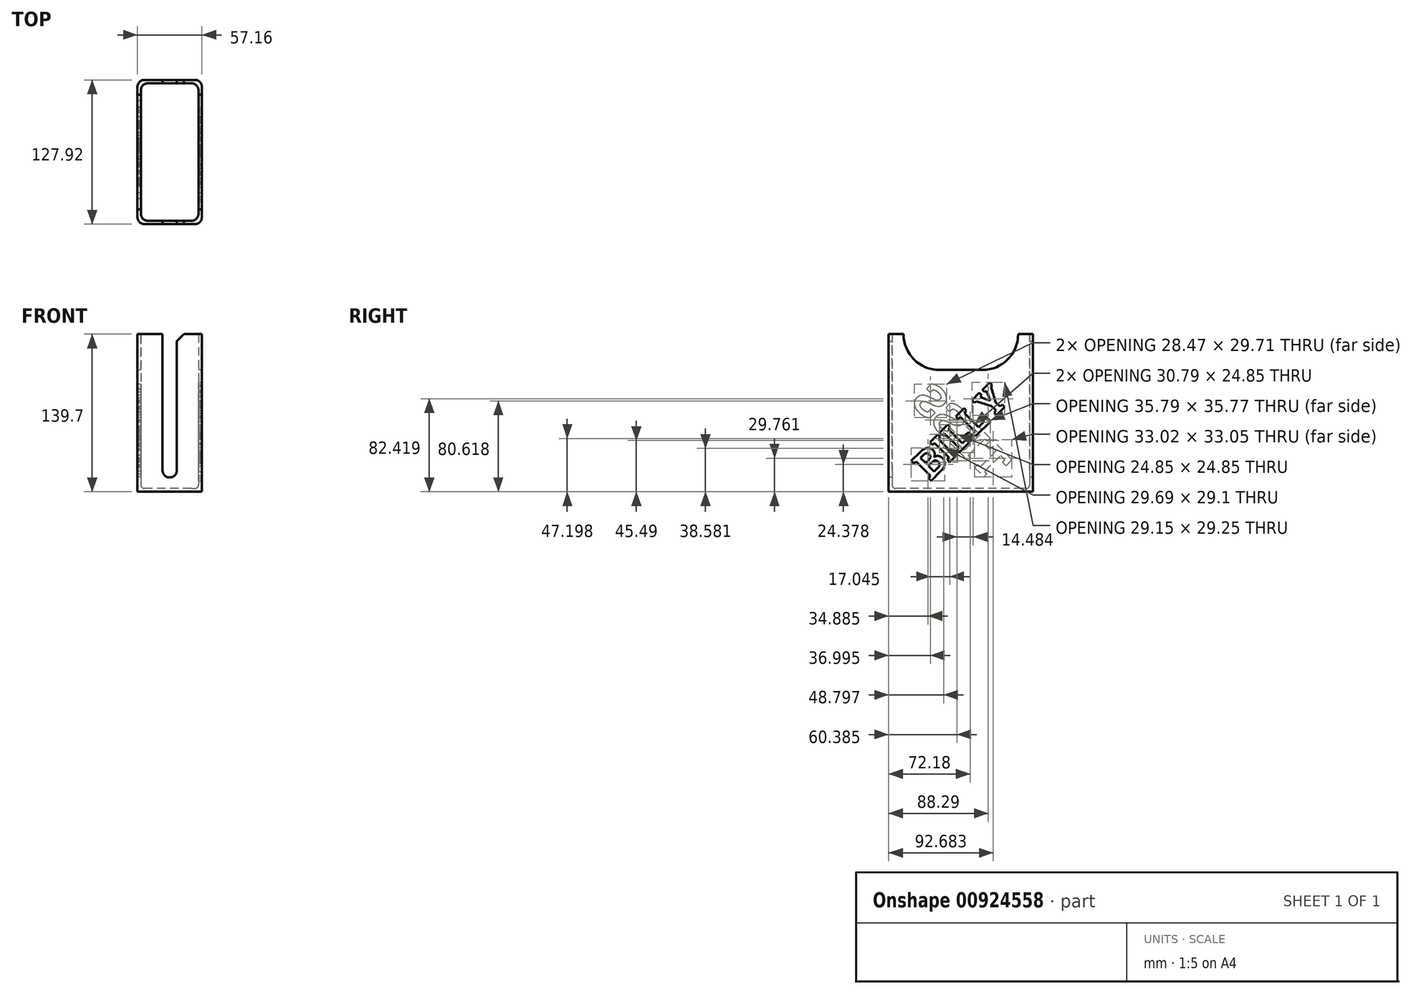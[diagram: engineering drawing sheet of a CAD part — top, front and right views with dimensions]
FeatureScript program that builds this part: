
annotation { "Feature Type Name" : "Feature", "Feature Type Description" : "" }
export const myFeature = defineFeature(function(context is Context, id is Id, definition is map)
    precondition{}
    {
        {
            var Q0;
            Q0=qCreatedBy(makeId("Top.planeOp"),FACE);
            var sketch = newSketch(context, id + "F0", { "sketchPlane" : qUnion([Q0])});
            skLineSegment(sketch, "E0.bottom", {"start": v(28.58, 63.96) * mm, "end": v(-28.57, 63.96) * mm});
            skLineSegment(sketch, "E0.top", {"start": v(28.58, -63.96) * mm, "end": v(-28.58, -63.96) * mm});
            skLineSegment(sketch, "E0.left", {"start": v(28.58, 63.96) * mm, "end": v(28.58, -63.96) * mm});
            skLineSegment(sketch, "E0.right", {"start": v(-28.58, 63.96) * mm, "end": v(-28.58, -63.96) * mm});
            skPoint(sketch, "E0.middle", {"position": v(0, 0) * mm});
            skSolve(sketch);
        }
        {
            var Q0;
            Q0=makeQuery(id+"F0.imprint","IMPRINT",FACE,{"disambiguationData":[TD([[makeQuery(id+"F0.imprint","IMPRINT",EDGE,{"derivedFrom":sQuery(id+"F0.wireOp",EDGE,"E0.bottom")}),1.0]])]});
            extrude(context, id + "F1", {"entities" : qUnion([Q0]), "depth" : 139.7 * mm, "offsetDistance" : 25.4 * mm});
        }
        {
            var Q0;
            Q0=makeQuery(id+"F1.opExtrude","CAP_FACE",FACE,{"disambiguationData":[OSD([sQuery(id+"F0.wireOp",EDGE,"E0.bottom"),sQuery(id+"F0.wireOp",EDGE,"E0.top"),sQuery(id+"F0.wireOp",EDGE,"E0.left"),sQuery(id+"F0.wireOp",EDGE,"E0.right")])],"isStart":false});
            shell(context, id + "F2", {"entities" : qUnion([Q0]), "thickness" : 3 * mm});
        }
        {
            var Q0;
            Q0=makeQuery(id+"F1.opExtrude","CAP_FACE",FACE,{"disambiguationData":[OSD([sQuery(id+"F0.wireOp",EDGE,"E0.bottom"),sQuery(id+"F0.wireOp",EDGE,"E0.top"),sQuery(id+"F0.wireOp",EDGE,"E0.left"),sQuery(id+"F0.wireOp",EDGE,"E0.right")])],"isStart":false});
            var sketch = newSketch(context, id + "F3", { "sketchPlane" : qUnion([Q0])});
            skLineSegment(sketch, "E1.bottom", {"start": v(-6.35, 63.96) * mm, "end": v(6.35, 63.96) * mm});
            skLineSegment(sketch, "E1.top", {"start": v(-6.35, -63.96) * mm, "end": v(6.35, -63.96) * mm});
            skLineSegment(sketch, "E1.left", {"start": v(-6.35, 63.96) * mm, "end": v(-6.35, -63.96) * mm});
            skLineSegment(sketch, "E1.right", {"start": v(6.35, 63.96) * mm, "end": v(6.35, -63.96) * mm});
            skPoint(sketch, "E1.middle", {"position": v(0, 0) * mm});
            skSolve(sketch);
        }
        {
            var Q0;
            {var subQ0=sQuery(id+"F3.wireOp",EDGE,"E1.left");var subQ1=sQuery(id+"F0.wireOp",EDGE,"E0.bottom");var subQ2=makeQuery(id+"F2.opShell","OFFSET_EDGE",EDGE,{"disambiguationData":[OSD([subQ1]),TDD([makeQuery(id+"F1.opExtrude","CAP_EDGE",EDGE,{"disambiguationData":[OSD([subQ1])],"isStart":false})])]});var subQ3=makeQuery(id+"F3.imprint","INTERSECT",VERTEX,{"derivedFrom":[subQ2,subQ0]});Q0=makeQuery(id+"F3.imprint","IMPRINT",FACE,{"disambiguationData":[TD([[makeQuery(id+"F3.imprint","IMPRINT",EDGE,{"disambiguationData":[TD([[subQ3,-1.0]])],"derivedFrom":subQ0}),1.0]])]});}
            var Q1;
            {var subQ0=sQuery(id+"F3.wireOp",EDGE,"E1.top");Q1=makeQuery(id+"F3.imprint","IMPRINT",FACE,{"disambiguationData":[TD([[makeQuery(id+"F3.imprint","IMPRINT",EDGE,{"derivedFrom":subQ0}),-1.0]])]});}
            var Q2;
            {var subQ0=sQuery(id+"F3.wireOp",EDGE,"E1.bottom");Q2=makeQuery(id+"F3.imprint","IMPRINT",FACE,{"disambiguationData":[TD([[makeQuery(id+"F3.imprint","IMPRINT",EDGE,{"derivedFrom":subQ0}),1.0]])]});}
            var Q3;
            {var subQ7=sQuery(id+"F0.wireOp",EDGE,"E0.left");var subQ8=makeQuery(id+"F2.opShell","OFFSET_EDGE",EDGE,{"disambiguationData":[OSD([subQ7]),TDD([makeQuery(id+"F1.opExtrude","CAP_EDGE",EDGE,{"disambiguationData":[OSD([subQ7])],"isStart":false})])]});Q3=makeQuery(id+"F3.imprint","IMPRINT",FACE,{"disambiguationData":[TD([[makeQuery(id+"F3.imprint","IMPRINT",EDGE,{"derivedFrom":subQ8}),-1.0]])]});}
            var Q4;
            Q4=makeQuery(id+"F2.opShell","OFFSET_FACE",FACE,{"disambiguationData":[OSD([sQuery(id+"F0.wireOp",EDGE,"E0.bottom"),sQuery(id+"F0.wireOp",EDGE,"E0.top"),sQuery(id+"F0.wireOp",EDGE,"E0.left"),sQuery(id+"F0.wireOp",EDGE,"E0.right")])]});
            extrude(context, id + "F4", {"entities" : qUnion([Q0, Q1, Q2, Q3]), "operationType" : NewBodyOperationType.REMOVE, "oppositeDirection" : true, "depth" : 127 * mm, "endBoundEntityFace" : qUnion([Q4]), "offsetDistance" : 25.4 * mm});
        }
        {
            var Q0;
            {var subQ0=sQuery(id+"F3.wireOp",EDGE,"E1.left");var subQ2=sQuery(id+"F0.wireOp",EDGE,"E0.top");Q0=makeQuery(id+"F4.boolean.opBoolean","COPY",EDGE,{"disambiguationData":[TD([makeQuery(id+"F1.opExtrude","SWEPT_FACE",FACE,{"disambiguationData":[OSD([subQ2])]})])],"derivedFrom":makeQuery(id+"F4.opExtrude","CAP_EDGE",EDGE,{"disambiguationData":[OSD([subQ0])],"isStart":false})});}
            var Q1;
            {var subQ0=sQuery(id+"F3.wireOp",EDGE,"E1.right");var subQ1=sQuery(id+"F0.wireOp",EDGE,"E0.top");var subQ2=makeQuery(id+"F1.opExtrude","CAP_EDGE",EDGE,{"disambiguationData":[OSD([subQ1])],"isStart":false});Q1=makeQuery(id+"F4.boolean.opBoolean","COPY",EDGE,{"derivedFrom":makeQuery(id+"F4.opExtrude","CAP_EDGE",EDGE,{"disambiguationData":[OSD([subQ0]),TDD([makeQuery(id+"F3.imprint","IMPRINT",EDGE,{"disambiguationData":[TD([[makeQuery(id+"F3.imprint","INTERSECT",VERTEX,{"derivedFrom":[makeQuery(id+"F2.opShell","OFFSET_EDGE",EDGE,{"disambiguationData":[OSD([subQ1]),TDD([subQ2])]}),subQ0]}),-1.0]])],"derivedFrom":subQ0})])],"isStart":false})});}
            var Q2;
            {var subQ2=sQuery(id+"F0.wireOp",EDGE,"E0.bottom");var subQ3=sQuery(id+"F3.wireOp",EDGE,"E1.left");Q2=makeQuery(id+"F4.boolean.opBoolean","COPY",EDGE,{"disambiguationData":[TD([makeQuery(id+"F1.opExtrude","SWEPT_FACE",FACE,{"disambiguationData":[OSD([subQ2])]})])],"derivedFrom":makeQuery(id+"F4.opExtrude","CAP_EDGE",EDGE,{"disambiguationData":[OSD([subQ3])],"isStart":false})});}
            var Q3;
            {var subQ0=sQuery(id+"F3.wireOp",EDGE,"E1.right");var subQ1=sQuery(id+"F0.wireOp",EDGE,"E0.bottom");var subQ2=makeQuery(id+"F1.opExtrude","CAP_EDGE",EDGE,{"disambiguationData":[OSD([subQ1])],"isStart":false});Q3=makeQuery(id+"F4.boolean.opBoolean","COPY",EDGE,{"derivedFrom":makeQuery(id+"F4.opExtrude","CAP_EDGE",EDGE,{"disambiguationData":[OSD([subQ0]),TDD([makeQuery(id+"F3.imprint","IMPRINT",EDGE,{"disambiguationData":[TD([[makeQuery(id+"F3.imprint","INTERSECT",VERTEX,{"derivedFrom":[makeQuery(id+"F2.opShell","OFFSET_EDGE",EDGE,{"disambiguationData":[OSD([subQ1]),TDD([subQ2])]}),subQ0]}),1.0]])],"derivedFrom":subQ0})])],"isStart":false})});}
            fillet(context, id + "F5", {"entities" : qUnion([Q0, Q1, Q2, Q3]), "radius" : 6.35 * mm, "tangentPropagation" : true, "allowEdgeOverflow" : false});
        }
        {
            var Q0;
            Q0=makeQuery(id+"F1.opExtrude","SWEPT_FACE",FACE,{"disambiguationData":[OSD([sQuery(id+"F0.wireOp",EDGE,"E0.right")])]});
            var sketch = newSketch(context, id + "F6", { "sketchPlane" : qUnion([Q0])});
            skLineSegment(sketch, "E2.bottom", {"start": v(50.8, 107.95) * mm, "end": v(-50.8, 107.95) * mm});
            skLineSegment(sketch, "E2.top", {"start": v(50.8, 139.7) * mm, "end": v(-50.8, 139.7) * mm});
            skLineSegment(sketch, "E2.left", {"start": v(50.8, 107.95) * mm, "end": v(50.8, 139.7) * mm});
            skLineSegment(sketch, "E2.right", {"start": v(-50.8, 107.95) * mm, "end": v(-50.8, 139.7) * mm});
            skPoint(sketch, "E2.middle", {"position": v(0, 123.83) * mm});
            skSolve(sketch);
        }
        {
            var Q0;
            {var subQ0=sQuery(id+"F6.wireOp",EDGE,"E2.top");Q0=makeQuery(id+"F6.imprint","IMPRINT",FACE,{"disambiguationData":[TD([[makeQuery(id+"F6.imprint","IMPRINT",EDGE,{"derivedFrom":subQ0}),1.0]])]});}
            var Q1;
            {var subQ0=sQuery(id+"F6.wireOp",EDGE,"E2.bottom");Q1=makeQuery(id+"F6.imprint","IMPRINT",FACE,{"disambiguationData":[TD([[makeQuery(id+"F6.imprint","IMPRINT",EDGE,{"derivedFrom":subQ0}),-1.0]])]});}
            extrude(context, id + "F7", {"entities" : qUnion([Q0, Q1]), "operationType" : NewBodyOperationType.REMOVE, "endBound" : BoundingType.THROUGH_ALL, "oppositeDirection" : true, "depth" : 25.4 * mm, "offsetDistance" : 25.4 * mm});
        }
        {
            var Q0;
            {var subQ0=sQuery(id+"F0.wireOp",EDGE,"E0.right");var subQ1=sQuery(id+"F6.wireOp",EDGE,"E2.bottom");var subQ2=sQuery(id+"F6.wireOp",EDGE,"E2.right");Q0=makeQuery(id+"F7.boolean.opBoolean","COPY",EDGE,{"disambiguationData":[TD([makeQuery(id+"F1.opExtrude","SWEPT_FACE",FACE,{"disambiguationData":[OSD([subQ0])]})])],"derivedFrom":makeQuery(id+"F7.opExtrude","SWEPT_EDGE",EDGE,{"disambiguationData":[OSD([subQ1,subQ2])]})});}
            var Q1;
            {var subQ0=sQuery(id+"F0.wireOp",EDGE,"E0.left");var subQ1=sQuery(id+"F6.wireOp",EDGE,"E2.bottom");var subQ2=sQuery(id+"F6.wireOp",EDGE,"E2.right");Q1=makeQuery(id+"F7.boolean.opBoolean","COPY",EDGE,{"disambiguationData":[TD([makeQuery(id+"F1.opExtrude","SWEPT_FACE",FACE,{"disambiguationData":[OSD([subQ0])]})])],"derivedFrom":makeQuery(id+"F7.opExtrude","SWEPT_EDGE",EDGE,{"disambiguationData":[OSD([subQ1,subQ2])]})});}
            var Q2;
            {var subQ0=sQuery(id+"F0.wireOp",EDGE,"E0.left");var subQ1=sQuery(id+"F6.wireOp",EDGE,"E2.bottom");var subQ2=sQuery(id+"F6.wireOp",EDGE,"E2.left");Q2=makeQuery(id+"F7.boolean.opBoolean","COPY",EDGE,{"disambiguationData":[TD([makeQuery(id+"F1.opExtrude","SWEPT_FACE",FACE,{"disambiguationData":[OSD([subQ0])]})])],"derivedFrom":makeQuery(id+"F7.opExtrude","SWEPT_EDGE",EDGE,{"disambiguationData":[OSD([subQ1,subQ2])]})});}
            var Q3;
            {var subQ0=sQuery(id+"F0.wireOp",EDGE,"E0.right");var subQ1=sQuery(id+"F6.wireOp",EDGE,"E2.bottom");var subQ2=sQuery(id+"F6.wireOp",EDGE,"E2.left");Q3=makeQuery(id+"F7.boolean.opBoolean","COPY",EDGE,{"disambiguationData":[TD([makeQuery(id+"F1.opExtrude","SWEPT_FACE",FACE,{"disambiguationData":[OSD([subQ0])]})])],"derivedFrom":makeQuery(id+"F7.opExtrude","SWEPT_EDGE",EDGE,{"disambiguationData":[OSD([subQ1,subQ2])]})});}
            fillet(context, id + "F8", {"entities" : qUnion([Q0, Q1, Q2, Q3]), "radius" : 31.75 * mm, "tangentPropagation" : true, "allowEdgeOverflow" : false});
        }
        {
            var Q0;
            {var subQ0=sQuery(id+"F0.wireOp",EDGE,"E0.right");Q0=makeQuery(id+"F2.opShell","OFFSET_EDGE",EDGE,{"disambiguationData":[OSD([subQ0]),TDD([makeQuery(id+"F1.opExtrude","CAP_EDGE",EDGE,{"disambiguationData":[OSD([subQ0])],"isStart":true})])]});}
            var Q1;
            {var subQ0=sQuery(id+"F0.wireOp",EDGE,"E0.right");var subQ3=sQuery(id+"F0.wireOp",EDGE,"E0.bottom");Q1=makeQuery(id+"F4.boolean.opBoolean","SPLIT",EDGE,{"disambiguationData":[TD([makeQuery(id+"F2.opShell","OFFSET_FACE",FACE,{"disambiguationData":[OSD([subQ0])]})])],"derivedFrom":makeQuery(id+"F2.opShell","OFFSET_EDGE",EDGE,{"disambiguationData":[OSD([subQ3]),TDD([makeQuery(id+"F1.opExtrude","CAP_EDGE",EDGE,{"disambiguationData":[OSD([subQ3])],"isStart":true})])]})});}
            var Q2;
            {var subQ0=sQuery(id+"F0.wireOp",EDGE,"E0.left");Q2=makeQuery(id+"F2.opShell","OFFSET_EDGE",EDGE,{"disambiguationData":[OSD([subQ0]),TDD([makeQuery(id+"F1.opExtrude","CAP_EDGE",EDGE,{"disambiguationData":[OSD([subQ0])],"isStart":true})])]});}
            var Q3;
            {var subQ2=sQuery(id+"F0.wireOp",EDGE,"E0.left");var subQ3=sQuery(id+"F0.wireOp",EDGE,"E0.top");Q3=makeQuery(id+"F4.boolean.opBoolean","SPLIT",EDGE,{"disambiguationData":[TD([makeQuery(id+"F2.opShell","OFFSET_FACE",FACE,{"disambiguationData":[OSD([subQ2])]})])],"derivedFrom":makeQuery(id+"F2.opShell","OFFSET_EDGE",EDGE,{"disambiguationData":[OSD([subQ3]),TDD([makeQuery(id+"F1.opExtrude","CAP_EDGE",EDGE,{"disambiguationData":[OSD([subQ3])],"isStart":true})])]})});}
            fillet(context, id + "F9", {"entities" : qUnion([Q0, Q1, Q2, Q3]), "radius" : 3.17 * mm, "tangentPropagation" : true, "allowEdgeOverflow" : false});
        }
        {
            var Q0;
            {var subQ0=sQuery(id+"F0.wireOp",EDGE,"E0.right");var subQ1=sQuery(id+"F0.wireOp",EDGE,"E0.top");Q0=makeQuery(id+"FaH29F3IyYW9KPR_1.boolean.opBoolean","MERGE",EDGE,{"derivedFrom":[makeQuery(id+"F1.opExtrude","SWEPT_EDGE",EDGE,{"disambiguationData":[OSD([subQ1,subQ0])]}),makeQuery(id+"FaH29F3IyYW9KPR_1.opExtrude","SWEPT_EDGE",EDGE,{"disambiguationData":[OSD([subQ1,subQ0])]})]});}
            var Q1;
            {var subQ0=sQuery(id+"F0.wireOp",EDGE,"E0.left");var subQ1=sQuery(id+"F0.wireOp",EDGE,"E0.top");Q1=makeQuery(id+"FaH29F3IyYW9KPR_1.boolean.opBoolean","MERGE",EDGE,{"derivedFrom":[makeQuery(id+"F1.opExtrude","SWEPT_EDGE",EDGE,{"disambiguationData":[OSD([subQ1,subQ0])]}),makeQuery(id+"FaH29F3IyYW9KPR_1.opExtrude","SWEPT_EDGE",EDGE,{"disambiguationData":[OSD([subQ1,subQ0])]})]});}
            var Q2;
            {var subQ0=sQuery(id+"F0.wireOp",EDGE,"E0.left");var subQ1=sQuery(id+"F0.wireOp",EDGE,"E0.bottom");Q2=makeQuery(id+"FaH29F3IyYW9KPR_1.boolean.opBoolean","MERGE",EDGE,{"derivedFrom":[makeQuery(id+"F1.opExtrude","SWEPT_EDGE",EDGE,{"disambiguationData":[OSD([subQ1,subQ0])]}),makeQuery(id+"FaH29F3IyYW9KPR_1.opExtrude","SWEPT_EDGE",EDGE,{"disambiguationData":[OSD([subQ1,subQ0])]})]});}
            var Q3;
            {var subQ0=sQuery(id+"F0.wireOp",EDGE,"E0.right");var subQ1=sQuery(id+"F0.wireOp",EDGE,"E0.bottom");Q3=makeQuery(id+"FaH29F3IyYW9KPR_1.boolean.opBoolean","MERGE",EDGE,{"derivedFrom":[makeQuery(id+"F1.opExtrude","SWEPT_EDGE",EDGE,{"disambiguationData":[OSD([subQ1,subQ0])]}),makeQuery(id+"FaH29F3IyYW9KPR_1.opExtrude","SWEPT_EDGE",EDGE,{"disambiguationData":[OSD([subQ1,subQ0])]})]});}
            var Q4;
            Q4=makeQuery(id+"F2.opShell","OFFSET_EDGE",EDGE,{"disambiguationData":[OSD([sQuery(id+"F0.wireOp",EDGE,"E0.bottom"),sQuery(id+"F0.wireOp",EDGE,"E0.right")])]});
            var Q5;
            Q5=makeQuery(id+"F2.opShell","OFFSET_EDGE",EDGE,{"disambiguationData":[OSD([sQuery(id+"F0.wireOp",EDGE,"E0.bottom"),sQuery(id+"F0.wireOp",EDGE,"E0.left")])]});
            var Q6;
            Q6=makeQuery(id+"F2.opShell","OFFSET_EDGE",EDGE,{"disambiguationData":[OSD([sQuery(id+"F0.wireOp",EDGE,"E0.top"),sQuery(id+"F0.wireOp",EDGE,"E0.right")])]});
            var Q7;
            Q7=makeQuery(id+"F2.opShell","OFFSET_EDGE",EDGE,{"disambiguationData":[OSD([sQuery(id+"F0.wireOp",EDGE,"E0.top"),sQuery(id+"F0.wireOp",EDGE,"E0.left")])]});
            fillet(context, id + "F10", {"entities" : qUnion([Q0, Q1, Q2, Q3, Q4, Q5, Q6, Q7]), "radius" : 6.35 * mm, "tangentPropagation" : true, "allowEdgeOverflow" : false});
        }
        {
            var Q0;
            {var subQ0=sQuery(id+"F0.wireOp",EDGE,"E0.top");var subQ1=sQuery(id+"F3.wireOp",EDGE,"E1.left");Q0=makeQuery(id+"F4.boolean.opBoolean","COPY",EDGE,{"disambiguationData":[TD([makeQuery(id+"F1.opExtrude","SWEPT_FACE",FACE,{"disambiguationData":[OSD([subQ0])]})])],"derivedFrom":makeQuery(id+"F4.opExtrude","CAP_EDGE",EDGE,{"disambiguationData":[OSD([subQ1])],"isStart":true})});}
            var Q1;
            {var subQ0=sQuery(id+"F3.wireOp",EDGE,"E1.right");var subQ1=sQuery(id+"F0.wireOp",EDGE,"E0.top");var subQ2=makeQuery(id+"F1.opExtrude","CAP_EDGE",EDGE,{"disambiguationData":[OSD([subQ1])],"isStart":false});Q1=makeQuery(id+"F4.boolean.opBoolean","COPY",EDGE,{"derivedFrom":makeQuery(id+"F4.opExtrude","CAP_EDGE",EDGE,{"disambiguationData":[OSD([subQ0]),TDD([makeQuery(id+"F3.imprint","IMPRINT",EDGE,{"disambiguationData":[TD([[makeQuery(id+"F3.imprint","INTERSECT",VERTEX,{"derivedFrom":[makeQuery(id+"F2.opShell","OFFSET_EDGE",EDGE,{"disambiguationData":[OSD([subQ1]),TDD([subQ2])]}),subQ0]}),-1.0]])],"derivedFrom":subQ0})])],"isStart":true})});}
            var Q2;
            {var subQ0=sQuery(id+"F0.wireOp",EDGE,"E0.bottom");var subQ1=sQuery(id+"F3.wireOp",EDGE,"E1.left");Q2=makeQuery(id+"F4.boolean.opBoolean","COPY",EDGE,{"disambiguationData":[TD([makeQuery(id+"F1.opExtrude","SWEPT_FACE",FACE,{"disambiguationData":[OSD([subQ0])]})])],"derivedFrom":makeQuery(id+"F4.opExtrude","CAP_EDGE",EDGE,{"disambiguationData":[OSD([subQ1])],"isStart":true})});}
            var Q3;
            {var subQ0=sQuery(id+"F3.wireOp",EDGE,"E1.right");var subQ1=sQuery(id+"F0.wireOp",EDGE,"E0.bottom");var subQ2=makeQuery(id+"F1.opExtrude","CAP_EDGE",EDGE,{"disambiguationData":[OSD([subQ1])],"isStart":false});Q3=makeQuery(id+"F4.boolean.opBoolean","COPY",EDGE,{"derivedFrom":makeQuery(id+"F4.opExtrude","CAP_EDGE",EDGE,{"disambiguationData":[OSD([subQ0]),TDD([makeQuery(id+"F3.imprint","IMPRINT",EDGE,{"disambiguationData":[TD([[makeQuery(id+"F3.imprint","INTERSECT",VERTEX,{"derivedFrom":[makeQuery(id+"F2.opShell","OFFSET_EDGE",EDGE,{"disambiguationData":[OSD([subQ1]),TDD([subQ2])]}),subQ0]}),1.0]])],"derivedFrom":subQ0})])],"isStart":true})});}
            chamfer(context, id + "F11", {"entities" : qUnion([Q0, Q1, Q2, Q3]), "width" : 6.35 * mm, "tangentPropagation" : true});
        }
        {
            var Q0;
            Q0=makeQuery(id+"F1.opExtrude","SWEPT_FACE",FACE,{"disambiguationData":[OSD([sQuery(id+"F0.wireOp",EDGE,"E0.left")])]});
            var sketch = newSketch(context, id + "F12", { "sketchPlane" : qUnion([Q0])});
            skText(sketch, "E3", { "text": "BILLY", "fontName": "RobotoSlab-Bold.ttf"});
            skPoint(sketch, "E4", {"position": v(0, 53.98) * mm});
            skLineSegment(sketch, "E5", {"start": v(0, 107.95) * mm, "end": v(0, 0) * mm, "construction": true});
            skLineSegment(sketch, "E6", {"start": v(0, 53.98) * mm, "end": v(-57.6, 53.98) * mm, "construction": true});
            skLineSegment(sketch, "E7", {"start": v(0, 53.98) * mm, "end": v(57.6, 53.98) * mm, "construction": true});
            const initialGuessF12  = {"E3": [-0.02702, 0.00915, 0.7071, 0.7071, 0.02517]};
            skSetInitialGuess(sketch, initialGuessF12);
            skSolve(sketch);
        }
        {
            var Q0;
            Q0 = qSketchRegion(id + "F12", true);
            var Q1;
            Q1=makeQuery(id+"F2.opShell","OFFSET_FACE",FACE,{"disambiguationData":[OSD([sQuery(id+"F0.wireOp",EDGE,"E0.left")])]});
            extrude(context, id + "F13", {"entities" : qUnion([Q0]), "operationType" : NewBodyOperationType.REMOVE, "endBound" : BoundingType.UP_TO_SURFACE, "oppositeDirection" : true, "depth" : 25.4 * mm, "endBoundEntityFace" : qUnion([Q1]), "offsetDistance" : 25.4 * mm});
        }
        {
            var Q0;
            Q0=makeQuery(id+"F1.opExtrude","SWEPT_FACE",FACE,{"disambiguationData":[OSD([sQuery(id+"F0.wireOp",EDGE,"E0.right")])]});
            var sketch = newSketch(context, id + "F14", { "sketchPlane" : qUnion([Q0])});
            skText(sketch, "E8", { "text": "TESS", "fontName": "RobotoSlab-Bold.ttf"});
            skPoint(sketch, "E9", {"position": v(0, 53.98) * mm});
            skLineSegment(sketch, "E10", {"start": v(0, 107.95) * mm, "end": v(0, 0) * mm, "construction": true});
            skLineSegment(sketch, "E11", {"start": v(0, 53.98) * mm, "end": v(-57.6, 53.98) * mm, "construction": true});
            skLineSegment(sketch, "E12", {"start": v(0, 53.98) * mm, "end": v(57.6, 53.98) * mm, "construction": true});
            const initialGuessF14  = {"E8": [-0.0258, 0.00794, 0.7071, 0.7071, 0.02862]};
            skSetInitialGuess(sketch, initialGuessF14);
            skSolve(sketch);
        }
        {
            var Q0;
            Q0 = qSketchRegion(id + "F14", true);
            var Q1;
            Q1=makeQuery(id+"F2.opShell","OFFSET_FACE",FACE,{"disambiguationData":[OSD([sQuery(id+"F0.wireOp",EDGE,"E0.right")])]});
            extrude(context, id + "F15", {"entities" : qUnion([Q0]), "operationType" : NewBodyOperationType.REMOVE, "endBound" : BoundingType.UP_TO_SURFACE, "oppositeDirection" : true, "depth" : 25.4 * mm, "endBoundEntityFace" : qUnion([Q1]), "offsetDistance" : 25.4 * mm});
        }
        {
            var Q0;
            Q0 = qSketchRegion(id + "F12", true);
            var Q1;
            {var subQ0=sQuery(id+"F0.wireOp",EDGE,"E0.left");var subQ4=makeQuery(id+"F2.opShell","OFFSET_FACE",FACE,{"disambiguationData":[OSD([subQ0])]});Q1=makeQuery(id+"F13.boolean.opBoolean","SPLIT",FACE,{"disambiguationData":[TD([makeQuery(id+"F9.opFillet","BLEND_FACE",FACE,{"disambiguationData":[OSD([subQ0])]})])],"derivedFrom":subQ4});}
            extrude(context, id + "F16", {"entities" : qUnion([Q0]), "endBound" : BoundingType.UP_TO_SURFACE, "oppositeDirection" : true, "depth" : 25.4 * mm, "endBoundEntityFace" : qUnion([Q1]), "offsetDistance" : 25.4 * mm});
        }
        {
            var Q0;
            Q0 = qSketchRegion(id + "F14", true);
            var Q1;
            Q1=makeQuery(id+"F2.opShell","OFFSET_FACE",FACE,{"disambiguationData":[OSD([sQuery(id+"F0.wireOp",EDGE,"E0.right")])]});
            extrude(context, id + "F17", {"entities" : qUnion([Q0]), "endBound" : BoundingType.UP_TO_SURFACE, "oppositeDirection" : true, "depth" : 25.4 * mm, "endBoundEntityFace" : qUnion([Q1]), "offsetDistance" : 25.4 * mm});
        }
    });
